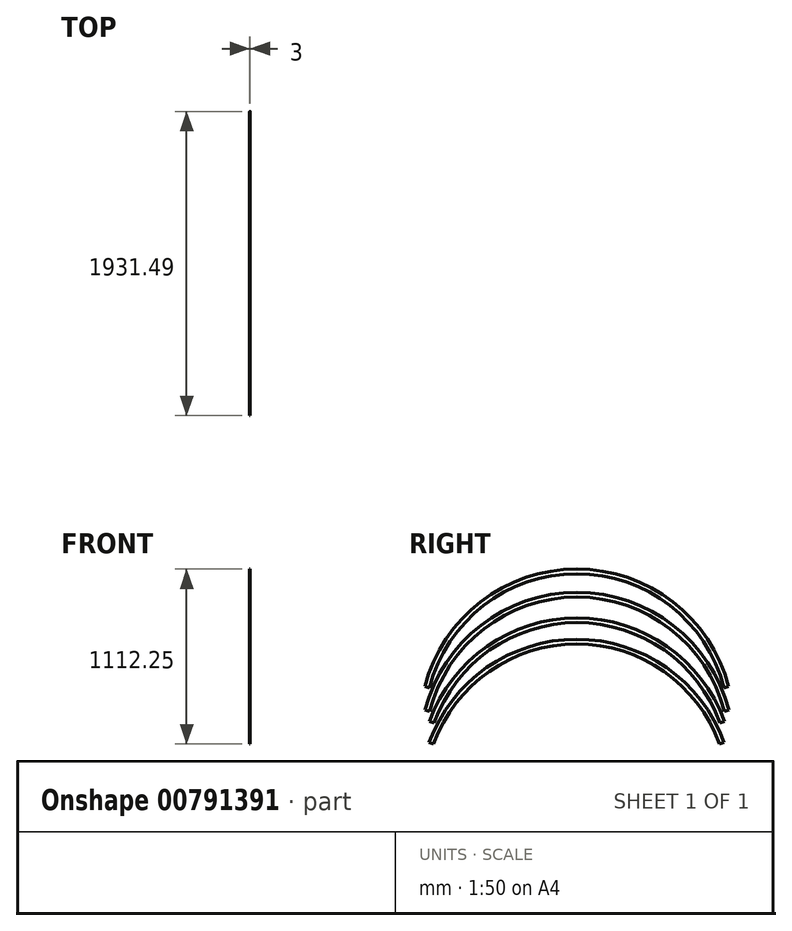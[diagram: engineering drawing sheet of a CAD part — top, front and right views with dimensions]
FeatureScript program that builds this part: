
annotation { "Feature Type Name" : "Feature", "Feature Type Description" : "" }
export const myFeature = defineFeature(function(context is Context, id is Id, definition is map)
    precondition{}
    {
        {
            var Q0;
            Q0=qCreatedBy(makeId("Right.planeOp"),FACE);
            var sketch = newSketch(context, id + "F0", { "sketchPlane" : qUnion([Q0])});
            skArc(sketch, "E0", {"start": v(922.48, 335.75) * mm, "mid": v(0, 981.68) * mm, "end": v(-922.48, 335.75) * mm, "construction": true});
            skLineSegment(sketch, "E1", {"start": v(0, 0) * mm, "end": v(922.48, 335.75) * mm, "construction": true});
            skLineSegment(sketch, "E2", {"start": v(0, 0) * mm, "end": v(-922.48, 335.75) * mm, "construction": true});
            skLineSegment(sketch, "E3", {"start": v(-908.38, 330.62) * mm, "end": v(-936.57, 340.88) * mm});
            skLineSegment(sketch, "E4", {"start": v(908.38, 330.62) * mm, "end": v(936.57, 340.88) * mm});
            skArc(sketch, "E5", {"start": v(-936.57, 340.88) * mm, "mid": v(0, 996.68) * mm, "end": v(936.57, 340.88) * mm});
            skArc(sketch, "E6", {"start": v(-908.38, 330.62) * mm, "mid": v(0, 966.68) * mm, "end": v(908.38, 330.62) * mm});
            skArc(sketch, "E7.0.1.0", {"start": v(-938.9, 205.3) * mm, "mid": v(-2.33, 861.1) * mm, "end": v(934.25, 205.3) * mm});
            skLineSegment(sketch, "E7.0.1.1", {"start": v(-910.7, 195.05) * mm, "end": v(-938.9, 205.3) * mm});
            skLineSegment(sketch, "E7.0.1.2", {"start": v(906.06, 195.05) * mm, "end": v(934.25, 205.3) * mm});
            skArc(sketch, "E7.0.1.3", {"start": v(-910.7, 195.05) * mm, "mid": v(-2.33, 831.1) * mm, "end": v(906.06, 195.05) * mm});
            skLineSegment(sketch, "E7.direction1", {"start": v(-936.57, 340.88) * mm, "end": v(-1482.36, 340.88) * mm, "construction": true});
            skLineSegment(sketch, "E7.direction2", {"start": v(-936.57, 340.88) * mm, "end": v(-938.9, 205.3) * mm, "construction": true});
            skSolve(sketch);
        }
        {
            var Q0;
            Q0 = qSketchRegion(id + "F0", true);
            extrude(context, id + "F1", {"entities" : qUnion([Q0]), "depth" : 3 * mm, "offsetDistance" : 25 * mm});
        }
        {
            var Q0;
            Q0=qCreatedBy(makeId("Right.planeOp"),FACE);
            var sketch = newSketch(context, id + "F2", { "sketchPlane" : qUnion([Q0])});
            skArc(sketch, "E8", {"start": v(950.41, 408.12) * mm, "mid": v(0, 1144) * mm, "end": v(-950.41, 408.12) * mm, "construction": true});
            skLineSegment(sketch, "E9", {"start": v(0, 162.32) * mm, "end": v(950.41, 408.12) * mm, "construction": true});
            skLineSegment(sketch, "E10", {"start": v(0, 162.32) * mm, "end": v(-950.41, 408.12) * mm, "construction": true});
            skLineSegment(sketch, "E11", {"start": v(-935.89, 404.36) * mm, "end": v(-964.93, 411.87) * mm});
            skLineSegment(sketch, "E12", {"start": v(935.89, 404.36) * mm, "end": v(964.93, 411.87) * mm});
            skArc(sketch, "E13", {"start": v(-935.89, 404.36) * mm, "mid": v(0, 1129) * mm, "end": v(935.89, 404.36) * mm});
            skArc(sketch, "E14", {"start": v(-964.93, 411.87) * mm, "mid": v(0, 1159) * mm, "end": v(964.93, 411.87) * mm});
            skArc(sketch, "E15.0.1.0", {"start": v(-937.52, 552.66) * mm, "mid": v(-1.63, 1277.3) * mm, "end": v(934.26, 552.66) * mm});
            skArc(sketch, "E15.0.1.1", {"start": v(-966.56, 560.17) * mm, "mid": v(-1.63, 1307.3) * mm, "end": v(963.3, 560.17) * mm});
            skLineSegment(sketch, "E15.0.1.2", {"start": v(934.26, 552.66) * mm, "end": v(963.3, 560.17) * mm});
            skLineSegment(sketch, "E15.0.1.3", {"start": v(-937.52, 552.66) * mm, "end": v(-966.56, 560.17) * mm});
            skLineSegment(sketch, "E15.direction1", {"start": v(-964.93, 411.87) * mm, "end": v(-948.69, 411.87) * mm, "construction": true});
            skLineSegment(sketch, "E15.direction2", {"start": v(-964.93, 411.87) * mm, "end": v(-966.56, 560.17) * mm, "construction": true});
            skSolve(sketch);
        }
        {
            var Q0;
            Q0 = qSketchRegion(id + "F2", true);
            extrude(context, id + "F3", {"entities" : qUnion([Q0]), "depth" : 3 * mm, "offsetDistance" : 25 * mm});
        }
    });
